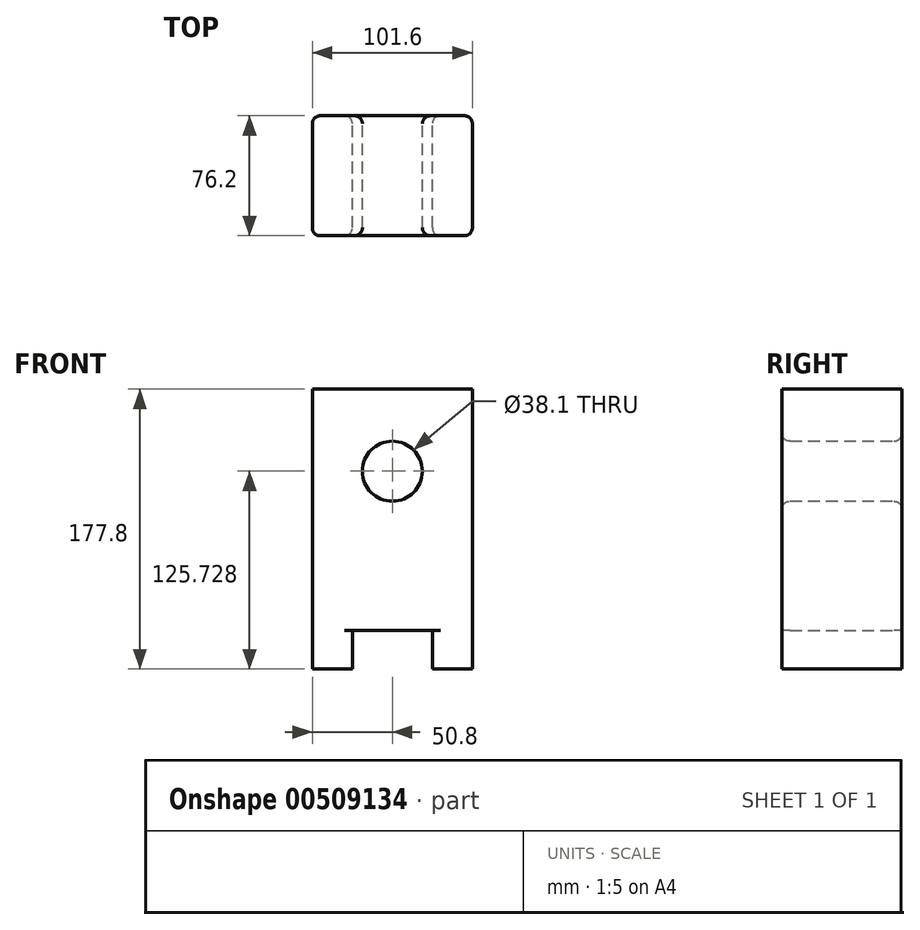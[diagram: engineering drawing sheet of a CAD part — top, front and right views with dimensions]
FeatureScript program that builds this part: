
annotation { "Feature Type Name" : "Feature", "Feature Type Description" : "" }
export const myFeature = defineFeature(function(context is Context, id is Id, definition is map)
    precondition{}
    {
        {
            var Q0;
            Q0=qCreatedBy(makeId("Front.planeOp"),FACE);
            var sketch = newSketch(context, id + "F0", { "sketchPlane" : qUnion([Q0])});
            skLineSegment(sketch, "E0.bottom", {"start": v(-50.8, 88.9) * mm, "end": v(50.8, 88.9) * mm});
            skLineSegment(sketch, "E0.top", {"start": v(-50.8, -88.9) * mm, "end": v(50.8, -88.9) * mm});
            skLineSegment(sketch, "E0.left", {"start": v(-50.8, 88.9) * mm, "end": v(-50.8, -88.9) * mm});
            skLineSegment(sketch, "E0.right", {"start": v(50.8, 88.9) * mm, "end": v(50.8, -88.9) * mm});
            skPoint(sketch, "E0.middle", {"position": v(0, 0) * mm});
            skCircle(sketch, "E1", {"center": v(0, 36.83) * mm, "radius": 19.05 * mm});
            skLineSegment(sketch, "E2.bottom", {"start": v(-25.4, -64.16) * mm, "end": v(25.4, -64.16) * mm});
            skLineSegment(sketch, "E2.top", {"start": v(-25.4, -89.56) * mm, "end": v(25.4, -89.56) * mm});
            skLineSegment(sketch, "E2.left", {"start": v(-25.4, -64.16) * mm, "end": v(-25.4, -89.56) * mm});
            skLineSegment(sketch, "E2.right", {"start": v(25.4, -64.16) * mm, "end": v(25.4, -89.56) * mm});
            skPoint(sketch, "E2.middle", {"position": v(0, -76.86) * mm});
            skSolve(sketch);
        }
        {
            var Q0;
            Q0=makeQuery(id+"F0.imprint","IMPRINT",FACE,{"disambiguationData":[TD([[makeQuery(id+"F0.imprint","IMPRINT",EDGE,{"derivedFrom":sQuery(id+"F0.wireOp",EDGE,"E0.bottom")}),-1.0]])]});
            extrude(context, id + "F1", {"entities" : qUnion([Q0]), "endBound" : BoundingType.SYMMETRIC, "depth" : 76.2 * mm});
        }
        {
            var Q0;
            Q0=makeQuery(id+"F1.opExtrude","CAP_EDGE",EDGE,{"disambiguationData":[OSD([sQuery(id+"F0.wireOp",EDGE,"E0.left")])],"isStart":true});
            var Q1;
            Q1=makeQuery(id+"F1.opExtrude","CAP_EDGE",EDGE,{"disambiguationData":[OSD([sQuery(id+"F0.wireOp",EDGE,"E0.right")])],"isStart":true});
            var Q2;
            Q2=makeQuery(id+"F1.opExtrude","CAP_EDGE",EDGE,{"disambiguationData":[OSD([sQuery(id+"F0.wireOp",EDGE,"E0.left")])],"isStart":false});
            var Q3;
            Q3=makeQuery(id+"F1.opExtrude","CAP_EDGE",EDGE,{"disambiguationData":[OSD([sQuery(id+"F0.wireOp",EDGE,"E0.right")])],"isStart":false});
            var Q4;
            Q4=makeQuery(id+"F1.opExtrude","CAP_EDGE",EDGE,{"disambiguationData":[OSD([sQuery(id+"F0.wireOp",EDGE,"E2.left")])],"isStart":false});
            var Q5;
            Q5=makeQuery(id+"F1.opExtrude","CAP_EDGE",EDGE,{"disambiguationData":[OSD([sQuery(id+"F0.wireOp",EDGE,"E2.right")])],"isStart":false});
            var Q6;
            Q6=makeQuery(id+"F1.opExtrude","CAP_EDGE",EDGE,{"disambiguationData":[OSD([sQuery(id+"F0.wireOp",EDGE,"E2.left")])],"isStart":true});
            var Q7;
            Q7=makeQuery(id+"F1.opExtrude","CAP_EDGE",EDGE,{"disambiguationData":[OSD([sQuery(id+"F0.wireOp",EDGE,"E2.right")])],"isStart":true});
            var Q8;
            Q8=makeQuery(id+"F1.opExtrude","CAP_EDGE",EDGE,{"disambiguationData":[OSD([sQuery(id+"F0.wireOp",EDGE,"E1")])],"isStart":false});
            var Q9;
            Q9=makeQuery(id+"F1.opExtrude","CAP_EDGE",EDGE,{"disambiguationData":[OSD([sQuery(id+"F0.wireOp",EDGE,"E1")])],"isStart":true});
            fillet(context, id + "F2", {"entities" : qUnion([Q0, Q1, Q2, Q3, Q4, Q5, Q6, Q7, Q8, Q9]), "radius" : 5.08 * mm, "tangentPropagation" : true, "allowEdgeOverflow" : false});
        }
    });
